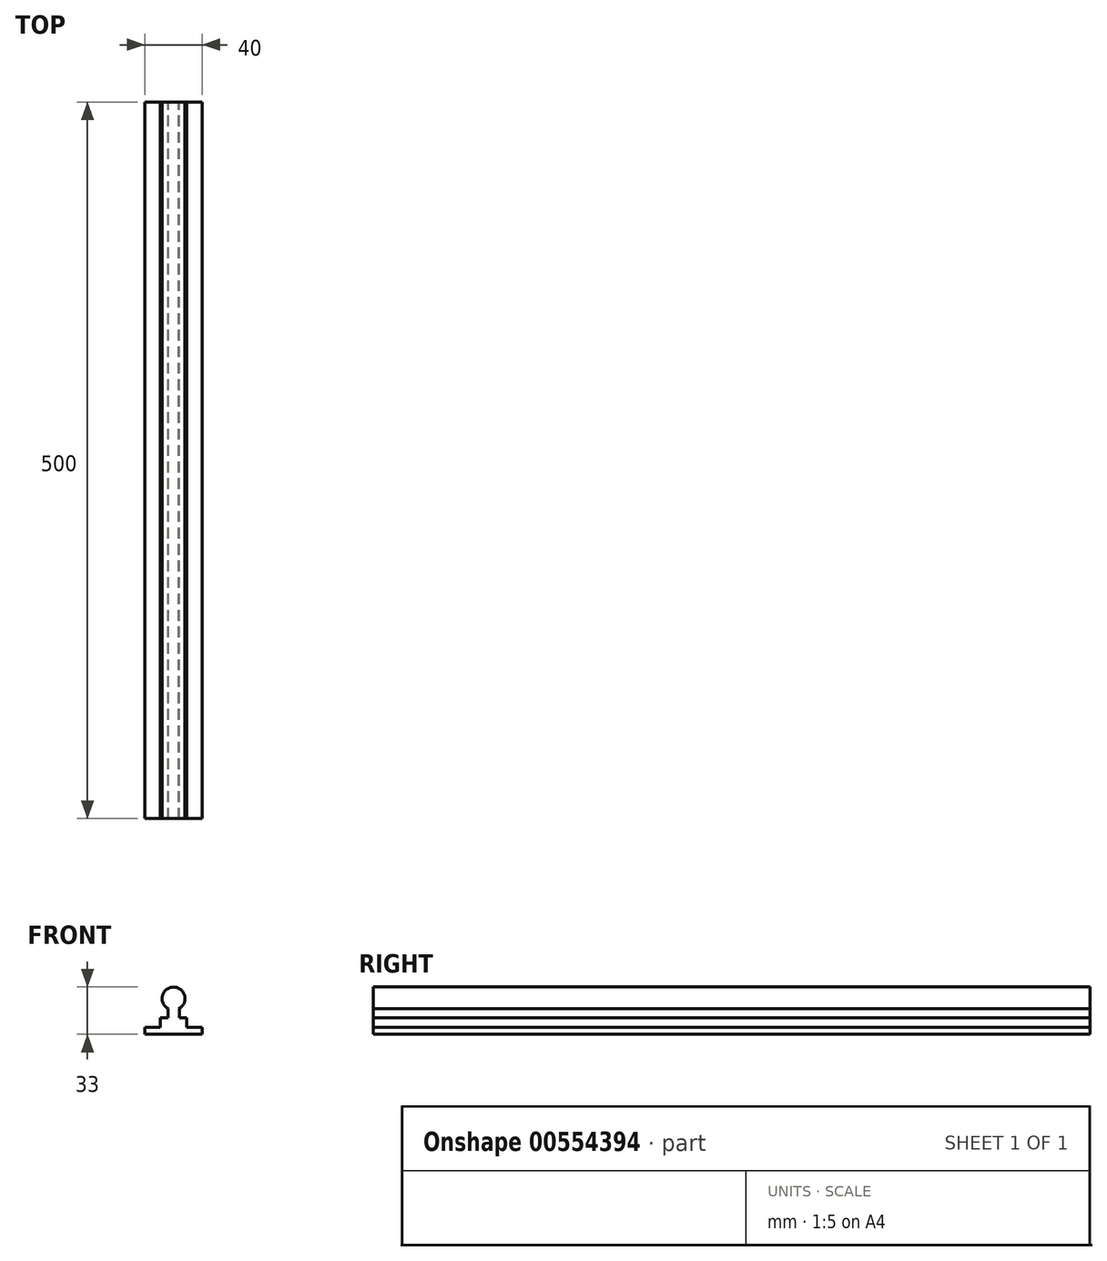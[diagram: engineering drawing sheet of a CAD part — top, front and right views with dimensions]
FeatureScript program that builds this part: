
annotation { "Feature Type Name" : "Feature", "Feature Type Description" : "" }
export const myFeature = defineFeature(function(context is Context, id is Id, definition is map)
    precondition{}
    {
        {
            var Q0;
            Q0=qCreatedBy(makeId("Front.planeOp"),FACE);
            var sketch = newSketch(context, id + "F0", { "sketchPlane" : qUnion([Q0])});
            skLineSegment(sketch, "E0.bottom", {"start": v(-34, -10.6) * mm, "end": v(6, -10.6) * mm});
            skLineSegment(sketch, "E0.top", {"start": v(-34, -5.6) * mm, "end": v(-23.24, -5.6) * mm});
            skLineSegment(sketch, "E0.left", {"start": v(-34, -10.6) * mm, "end": v(-34, -5.6) * mm});
            skLineSegment(sketch, "E0.right", {"start": v(6, -10.6) * mm, "end": v(6, -5.6) * mm});
            skArc(sketch, "E1", {"start": v(-10.5, 7.2) * mm, "mid": v(-14, 22.4) * mm, "end": v(-17.48, 7.2) * mm});
            skLineSegment(sketch, "E2.top", {"start": v(-23.24, 1.05) * mm, "end": v(-18, 1.05) * mm});
            skLineSegment(sketch, "E2.left", {"start": v(-23.24, -5.6) * mm, "end": v(-23.24, 1.05) * mm});
            skLineSegment(sketch, "E2.right", {"start": v(-4.74, -5.6) * mm, "end": v(-4.74, 1.05) * mm});
            skLineSegment(sketch, "E3", {"start": v(-14, 1.05) * mm, "end": v(-14, -5.6) * mm, "construction": true});
            skLineSegment(sketch, "E4.top", {"start": v(-18, 7.2) * mm, "end": v(-17.48, 7.2) * mm});
            skLineSegment(sketch, "E4.left", {"start": v(-18, 1.05) * mm, "end": v(-18, 7.2) * mm});
            skLineSegment(sketch, "E4.right", {"start": v(-10, 1.05) * mm, "end": v(-10, 7.2) * mm});
            skLineSegment(sketch, "E5.bottom", {"start": v(-14, 7.2) * mm, "end": v(-14, 7.2) * mm});
            skLineSegment(sketch, "E5.top", {"start": v(-14, 1.05) * mm, "end": v(-14, 1.05) * mm});
            skLineSegment(sketch, "E5.right", {"start": v(-14, 7.2) * mm, "end": v(-14, 1.05) * mm, "construction": true});
            skLineSegment(sketch, "E6.trimOffspring", {"start": v(-10, 1.05) * mm, "end": v(-4.74, 1.05) * mm});
            skLineSegment(sketch, "E7.trimOffspring", {"start": v(-4.74, -5.6) * mm, "end": v(6, -5.6) * mm});
            skLineSegment(sketch, "E8.trimOffspring", {"start": v(-10.5, 7.2) * mm, "end": v(-10, 7.2) * mm});
            skSolve(sketch);
        }
        {
            var Q0;
            Q0=makeQuery(id+"F0.imprint","IMPRINT",FACE,{"disambiguationData":[TD([[makeQuery(id+"F0.imprint","IMPRINT",EDGE,{"derivedFrom":sQuery(id+"F0.wireOp",EDGE,"E0.bottom")}),1.0]])]});
            extrude(context, id + "F1", {"entities" : qUnion([Q0]), "depth" : 500 * mm, "offsetDistance" : 25 * mm});
        }
    });
